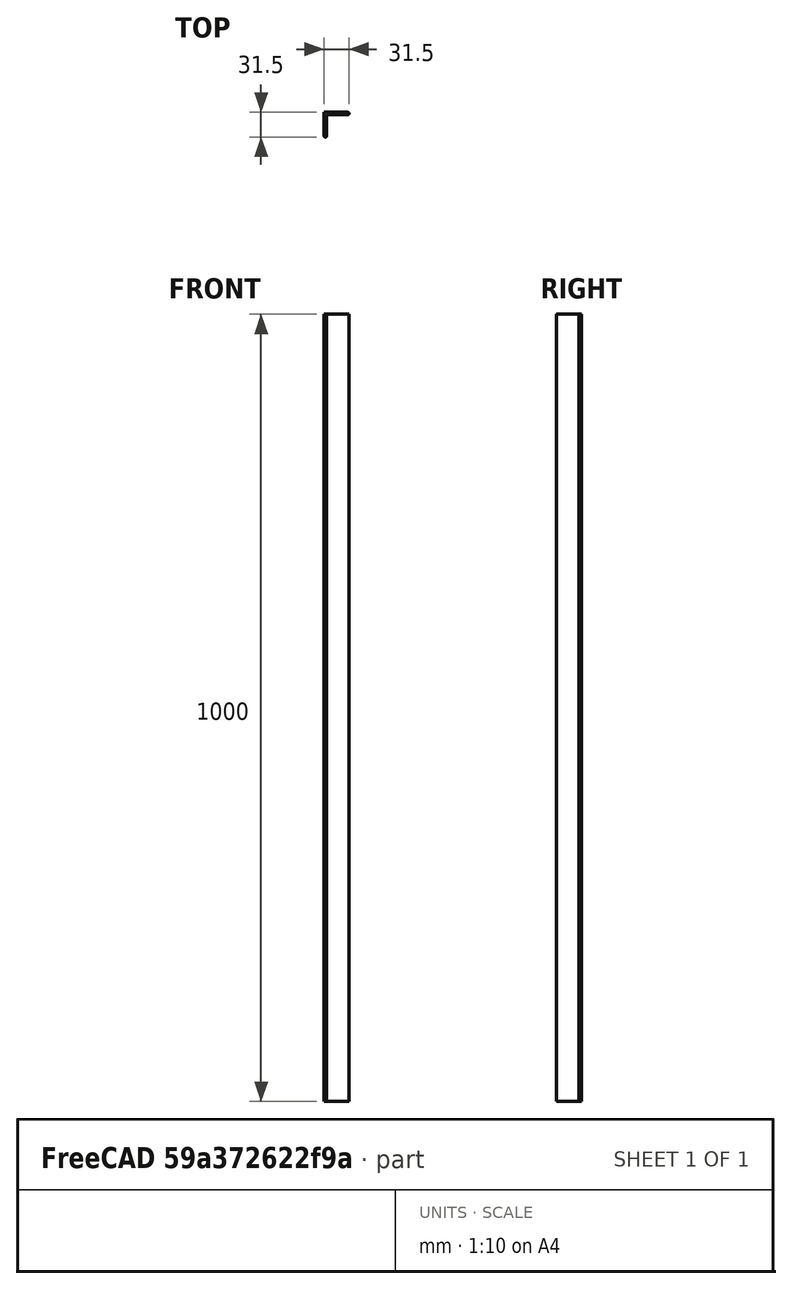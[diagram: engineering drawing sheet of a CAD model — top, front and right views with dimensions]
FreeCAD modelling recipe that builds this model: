
FCSTD DOCUMENT  (FreeCAD 0.18R4 (GitTag))
Label: TableJoint
License: All rights reserved
LicenseURL: http://en.wikipedia.org/wiki/All_rights_reserved
objects: Sketcher::SketchObject×1, PartDesign::Pad×1, PartDesign::Body×1
note: 4 computed .brp shape members not serialized (recipe doc carries the construction recipe); baked Part::Feature solids carry a one-line shape summary decoded from their .brp

FEATURE [Sketcher::SketchObject] Sketch
  sketch-geometry (6):
    g0: LineSegment StartX=-2.46519 StartY=-27.815 StartZ=0 EndX=-2.46519 EndY=2.18504 EndZ=0
    g1: LineSegment StartX=-2.46519 StartY=2.18504 StartZ=0 EndX=27.5348 EndY=2.18504 EndZ=0
    g2: LineSegment StartX=0.534809 StartY=-27.815 StartZ=0 EndX=0.534809 EndY=-0.814957 EndZ=0
    g3: LineSegment StartX=0.534809 StartY=-0.814957 StartZ=0 EndX=27.5348 EndY=-0.814957 EndZ=0
    g4: ArcOfCircle CenterX=27.5348 CenterY=0.685043 CenterZ=0 NormalX=0 NormalY=0 NormalZ=1 AngleXU=0 Radius=1.5 StartAngle=4.71239 EndAngle=7.85398
    g5: ArcOfCircle CenterX=-0.965191 CenterY=-27.815 CenterZ=0 NormalX=0 NormalY=0 NormalZ=1 AngleXU=0 Radius=1.5 StartAngle=3.14159 EndAngle=6.28319
  constraints (14):
    c: Coincident(g0,g1)
    c: Coincident(g2,g3)
    c: Horizontal(g3)
    c: Horizontal(g1)
    c: Vertical(g2)
    c: Vertical(g0)
    c: Tangent(g3,g4) = -1.5708
    c: Tangent(g1,g4) = 1.5708
    c: Tangent(g2,g5) = -1.5708
    c: Tangent(g0,g5) = 1.5708
    c: DistanceX(g0,g4) = 30
    c: Equal(g0,g1)
    c: Equal(g2,g3)
    c: Radius(g5) = 1.5
FEATURE [PartDesign::Pad] Pad
  Length = 1000
  Length2 = 100
  Profile = -> Sketch
  Type = 0
FEATURE [PartDesign::Body] Body
  Group = -> [Sketch,Pad]
  Origin = -> Origin
  Tip = -> Pad
